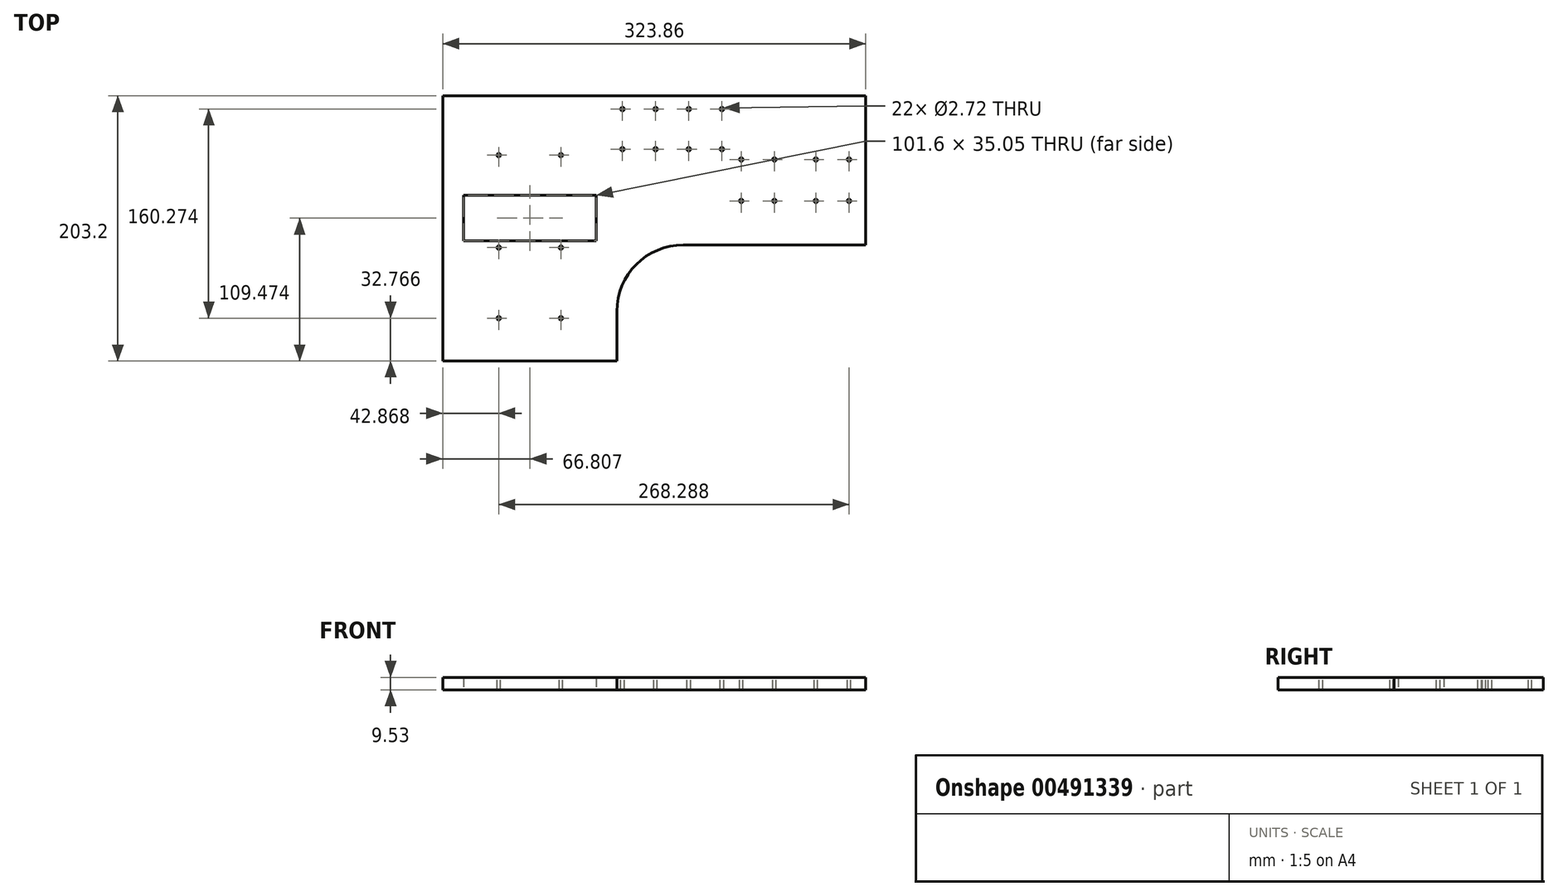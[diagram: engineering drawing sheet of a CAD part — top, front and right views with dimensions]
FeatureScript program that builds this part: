
annotation { "Feature Type Name" : "Feature", "Feature Type Description" : "" }
export const myFeature = defineFeature(function(context is Context, id is Id, definition is map)
    precondition{}
    {
        {
            var Q0;
            Q0=qCreatedBy(makeId("Top.planeOp"),FACE);
            var sketch = newSketch(context, id + "F0", { "sketchPlane" : qUnion([Q0])});
            skLineSegment(sketch, "E0.bottom", {"start": v(-161.93, 101.6) * mm, "end": v(161.92, 101.6) * mm});
            skLineSegment(sketch, "E0.top", {"start": v(-161.93, -101.6) * mm, "end": v(161.93, -101.6) * mm});
            skLineSegment(sketch, "E0.left", {"start": v(-161.93, 101.6) * mm, "end": v(-161.93, -101.6) * mm});
            skLineSegment(sketch, "E0.right", {"start": v(161.92, 101.6) * mm, "end": v(161.93, -101.6) * mm});
            skLineSegment(sketch, "E1.bottom", {"start": v(-145.92, 25.4) * mm, "end": v(-44.32, 25.4) * mm});
            skLineSegment(sketch, "E1.top", {"start": v(-145.92, -9.65) * mm, "end": v(-44.32, -9.65) * mm});
            skLineSegment(sketch, "E1.left", {"start": v(-145.92, 25.4) * mm, "end": v(-145.92, -9.65) * mm});
            skLineSegment(sketch, "E1.right", {"start": v(-44.32, 25.4) * mm, "end": v(-44.32, -9.65) * mm});
            skSolve(sketch);
        }
        {
            var Q0;
            Q0=makeQuery(id+"F0.imprint","IMPRINT",FACE,{"disambiguationData":[TD([[makeQuery(id+"F0.imprint","IMPRINT",EDGE,{"derivedFrom":sQuery(id+"F0.wireOp",EDGE,"E0.bottom")}),-1.0]])]});
            extrude(context, id + "F1", {"entities" : qUnion([Q0]), "depth" : 9.52 * mm});
        }
        {
            var Q0;
            Q0=makeQuery(id+"F1.opExtrude","CAP_FACE",FACE,{"disambiguationData":[OSD([sQuery(id+"F0.wireOp",EDGE,"E0.bottom"),sQuery(id+"F0.wireOp",EDGE,"E0.top"),sQuery(id+"F0.wireOp",EDGE,"E0.left"),sQuery(id+"F0.wireOp",EDGE,"E0.right"),sQuery(id+"F0.wireOp",EDGE,"E1.bottom"),sQuery(id+"F0.wireOp",EDGE,"E1.top"),sQuery(id+"F0.wireOp",EDGE,"E1.left"),sQuery(id+"F0.wireOp",EDGE,"E1.right")])],"isStart":false});
            var sketch = newSketch(context, id + "F2", { "sketchPlane" : qUnion([Q0])});
            skPoint(sketch, "E2", {"position": v(-119.06, 56.13) * mm});
            skPoint(sketch, "E3", {"position": v(-71.44, 56.13) * mm});
            skPoint(sketch, "E4", {"position": v(-119.06, -14.73) * mm});
            skPoint(sketch, "E5", {"position": v(-71.44, -14.73) * mm});
            skPoint(sketch, "E6", {"position": v(-119.06, -68.83) * mm});
            skPoint(sketch, "E7", {"position": v(-71.44, -68.83) * mm});
            skPoint(sketch, "E8", {"position": v(-24.34, 91.44) * mm});
            skPoint(sketch, "E9", {"position": v(-24.34, 60.7) * mm});
            skPoint(sketch, "E10", {"position": v(1.06, 91.44) * mm});
            skPoint(sketch, "E11", {"position": v(1.06, 60.7) * mm});
            skPoint(sketch, "E12", {"position": v(26.46, 91.44) * mm});
            skPoint(sketch, "E13", {"position": v(26.46, 60.7) * mm});
            skPoint(sketch, "E14", {"position": v(51.86, 91.44) * mm});
            skPoint(sketch, "E15", {"position": v(51.86, 60.7) * mm});
            skPoint(sketch, "E16", {"position": v(66.67, 52.83) * mm});
            skPoint(sketch, "E17", {"position": v(92.07, 52.83) * mm});
            skPoint(sketch, "E18", {"position": v(123.82, 52.83) * mm});
            skPoint(sketch, "E19", {"position": v(149.22, 52.83) * mm});
            skPoint(sketch, "E20", {"position": v(66.67, 21.08) * mm});
            skPoint(sketch, "E21", {"position": v(92.07, 21.08) * mm});
            skPoint(sketch, "E22", {"position": v(123.82, 21.08) * mm});
            skPoint(sketch, "E23", {"position": v(149.22, 21.08) * mm});
            skSolve(sketch);
        }
        {
            var Q0;
            Q0=sQuery(id+"F2.wireOp",VERTEX,"E2");
            var Q1;
            Q1=sQuery(id+"F2.wireOp",VERTEX,"E3");
            var Q2;
            Q2=sQuery(id+"F2.wireOp",VERTEX,"E4");
            var Q3;
            Q3=sQuery(id+"F2.wireOp",VERTEX,"E5");
            var Q4;
            Q4=sQuery(id+"F2.wireOp",VERTEX,"E6");
            var Q5;
            Q5=sQuery(id+"F2.wireOp",VERTEX,"E7");
            var Q6;
            Q6=sQuery(id+"F2.wireOp",VERTEX,"E9");
            var Q7;
            Q7=sQuery(id+"F2.wireOp",VERTEX,"E8");
            var Q8;
            Q8=sQuery(id+"F2.wireOp",VERTEX,"E10");
            var Q9;
            Q9=sQuery(id+"F2.wireOp",VERTEX,"E11");
            var Q10;
            Q10=sQuery(id+"F2.wireOp",VERTEX,"E13");
            var Q11;
            Q11=sQuery(id+"F2.wireOp",VERTEX,"E12");
            var Q12;
            Q12=sQuery(id+"F2.wireOp",VERTEX,"E14");
            var Q13;
            Q13=sQuery(id+"F2.wireOp",VERTEX,"E15");
            var Q14;
            Q14=sQuery(id+"F2.wireOp",VERTEX,"E16");
            var Q15;
            Q15=sQuery(id+"F2.wireOp",VERTEX,"E20");
            var Q16;
            Q16=sQuery(id+"F2.wireOp",VERTEX,"E21");
            var Q17;
            Q17=sQuery(id+"F2.wireOp",VERTEX,"E17");
            var Q18;
            Q18=sQuery(id+"F2.wireOp",VERTEX,"E18");
            var Q19;
            Q19=sQuery(id+"F2.wireOp",VERTEX,"E22");
            var Q20;
            Q20=sQuery(id+"F2.wireOp",VERTEX,"E17");
            var Q21;
            Q21=sQuery(id+"F2.wireOp",VERTEX,"E19");
            var Q22;
            Q22=sQuery(id+"F2.wireOp",VERTEX,"E23");
            var Q23;
            Q23=makeQuery(id+"F1.opExtrude","SWEPT_BODY",BODY,{"disambiguationData":[OSD([sQuery(id+"F0.wireOp",EDGE,"E0.bottom"),sQuery(id+"F0.wireOp",EDGE,"E0.top"),sQuery(id+"F0.wireOp",EDGE,"E0.left"),sQuery(id+"F0.wireOp",EDGE,"E0.right"),sQuery(id+"F0.wireOp",EDGE,"E1.bottom"),sQuery(id+"F0.wireOp",EDGE,"E1.top"),sQuery(id+"F0.wireOp",EDGE,"E1.left"),sQuery(id+"F0.wireOp",EDGE,"E1.right")])]});
            hole(context, id + "F3", {"style" : HoleStyle.SIMPLE, "endStyle" : HoleEndStyle.THROUGH, "holeDiameter" : 2.72 * mm, "isTappedThrough" : true, "tappedDepth" : 12.7 * mm, "tapClearance" : 3, "locations" : qUnion([Q0, Q1, Q2, Q3, Q4, Q5, Q6, Q7, Q8, Q9, Q10, Q11, Q12, Q13, Q14, Q15, Q16, Q17, Q18, Q19, Q20, Q21, Q22]), "scope" : qUnion([Q23])});
        }
        {
            var Q0;
            Q0=makeQuery(id+"F1.opExtrude","CAP_FACE",FACE,{"disambiguationData":[OSD([sQuery(id+"F0.wireOp",EDGE,"E0.bottom"),sQuery(id+"F0.wireOp",EDGE,"E0.top"),sQuery(id+"F0.wireOp",EDGE,"E0.left"),sQuery(id+"F0.wireOp",EDGE,"E0.right"),sQuery(id+"F0.wireOp",EDGE,"E1.bottom"),sQuery(id+"F0.wireOp",EDGE,"E1.top"),sQuery(id+"F0.wireOp",EDGE,"E1.left"),sQuery(id+"F0.wireOp",EDGE,"E1.right")])],"isStart":false});
            var sketch = newSketch(context, id + "F4", { "sketchPlane" : qUnion([Q0])});
            skLineSegment(sketch, "E24", {"start": v(161.93, -12.7) * mm, "end": v(22.22, -12.7) * mm});
            skLineSegment(sketch, "E25", {"start": v(-28.57, -63.5) * mm, "end": v(-28.57, -101.6) * mm});
            skLineSegment(sketch, "E26", {"start": v(-28.57, -101.6) * mm, "end": v(161.93, -101.6) * mm});
            skLineSegment(sketch, "E27", {"start": v(161.93, -101.6) * mm, "end": v(161.93, -12.7) * mm});
            skArc(sketch, "E28.filletArc", {"start": v(22.23, -12.7) * mm, "mid": v(-13.7, -27.58) * mm, "end": v(-28.57, -63.5) * mm});
            skSolve(sketch);
        }
        {
            var Q0;
            Q0=makeQuery(id+"F4.imprint","IMPRINT",FACE,{"disambiguationData":[TD([[makeQuery(id+"F4.imprint","IMPRINT",EDGE,{"derivedFrom":sQuery(id+"F4.wireOp",EDGE,"E24")}),1.0]])]});
            extrude(context, id + "F5", {"entities" : qUnion([Q0]), "operationType" : NewBodyOperationType.REMOVE, "endBound" : BoundingType.THROUGH_ALL, "oppositeDirection" : true, "depth" : 25.4 * mm});
        }
    });
